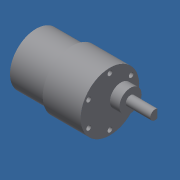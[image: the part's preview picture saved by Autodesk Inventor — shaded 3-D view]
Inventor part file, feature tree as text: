
AUTODESK INVENTOR PART (.ipt)
format: ipt  version: 2018 (Build 220112000, 112)  size: 132,608 bytes
history: native  units: mm
features: extrude x6, sketch x6
ambient origin geometry x8: Origin, YZ Plane, XZ Plane, XY Plane, X Axis, Y Axis, Z Axis, Center Point
bodies: Solid1 (feature_tree)
feature tree (12):
  extrude  "Extrusion1"  Depth=22.7mm TaperAngle=0.0deg
  extrude  "Extrusion2"  Depth=24.0mm TaperAngle=0.0deg
  extrude  "Extrusion3"  Depth=7.0mm
  extrude  "Extrusion4"  Depth=6.0mm
  extrude  "Extrusion5"  Depth=3.0mm
  extrude  "Extrusion6"  Depth=10.0mm TaperAngle=360.0deg
  sketch  "Sketch1"  dims[d0=33.0mm d1=22.7mm d2=0.0mm]
  sketch  "Sketch2"  dims[d3=37.0mm d4=24.0mm d5=0.0mm]
  sketch  "Sketch3"  dims[d6=14.0mm d7=7.0mm]
  sketch  "Sketch4"  dims[d8=6.0mm d9=0.0mm d10=6.0mm]
  sketch  "Sketch5"  dims[d11=15.5mm d12=0.0mm d13=3.0mm]
  sketch  "Sketch6"  dims[d14=15.5mm d15=60.0mm d17=360.0deg d19=10.0mm d20=0.0mm d21=10.0mm d22=0.0mm]
